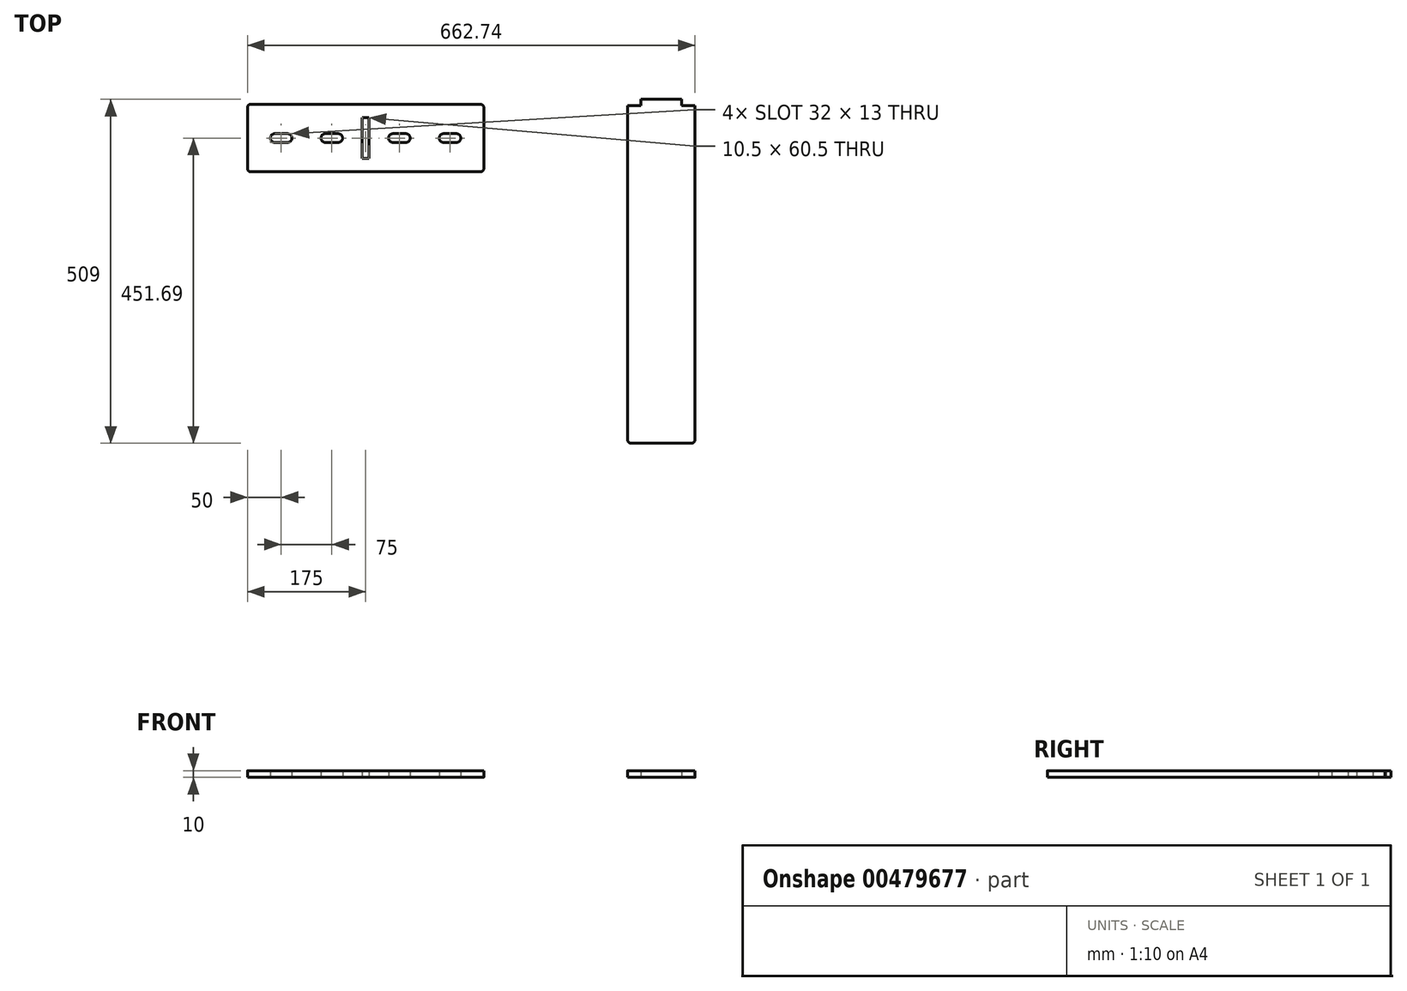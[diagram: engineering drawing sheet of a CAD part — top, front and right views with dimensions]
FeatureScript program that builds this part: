
annotation { "Feature Type Name" : "Feature", "Feature Type Description" : "" }
export const myFeature = defineFeature(function(context is Context, id is Id, definition is map)
    precondition{}
    {
        {
            var Q0;
            Q0=qCreatedBy(makeId("Top.planeOp"),FACE);
            var sketch = newSketch(context, id + "F0", { "sketchPlane" : qUnion([Q0])});
            skLineSegment(sketch, "E0.bottom", {"start": v(170, -50) * mm, "end": v(-170, -50) * mm});
            skLineSegment(sketch, "E0.top", {"start": v(170, 50) * mm, "end": v(-170, 50) * mm});
            skLineSegment(sketch, "E0.left", {"start": v(175, -45) * mm, "end": v(175, 45) * mm});
            skLineSegment(sketch, "E0.right", {"start": v(-175, -45) * mm, "end": v(-175, 45) * mm});
            skPoint(sketch, "E0.middle", {"position": v(0, 0) * mm});
            skLineSegment(sketch, "E1.bottom", {"start": v(-115.5, -6.5) * mm, "end": v(-134.5, -6.5) * mm});
            skLineSegment(sketch, "E1.top", {"start": v(-115.5, 6.5) * mm, "end": v(-134.5, 6.5) * mm});
            skPoint(sketch, "E1.middle", {"position": v(-125, 0) * mm});
            skArc(sketch, "E2", {"start": v(-134.5, 6.5) * mm, "mid": v(-141, 0) * mm, "end": v(-134.5, -6.5) * mm});
            skArc(sketch, "E3", {"start": v(-115.5, -6.5) * mm, "mid": v(-109, 0) * mm, "end": v(-115.5, 6.5) * mm});
            skLineSegment(sketch, "E4.1.0.0", {"start": v(-40.5, 6.5) * mm, "end": v(-59.5, 6.5) * mm});
            skArc(sketch, "E4.1.0.1", {"start": v(-40.5, -6.5) * mm, "mid": v(-34, 0) * mm, "end": v(-40.5, 6.5) * mm});
            skLineSegment(sketch, "E4.1.0.2", {"start": v(-40.5, -6.5) * mm, "end": v(-59.5, -6.5) * mm});
            skPoint(sketch, "E4.1.0.3", {"position": v(-50, 0) * mm});
            skArc(sketch, "E4.1.0.4", {"start": v(-59.5, 6.5) * mm, "mid": v(-66, 0) * mm, "end": v(-59.5, -6.5) * mm});
            skLineSegment(sketch, "E4.direction1", {"start": v(-134.5, -6.5) * mm, "end": v(-59.5, -6.5) * mm, "construction": true});
            skLineSegment(sketch, "E5", {"start": v(0, 50) * mm, "end": v(0, -50) * mm, "construction": true});
            skLineSegment(sketch, "E6", {"start": v(175, 0) * mm, "end": v(-175, 0) * mm, "construction": true});
            skLineSegment(sketch, "E7.bottom", {"start": v(134.5, -6.5) * mm, "end": v(115.5, -6.5) * mm});
            skLineSegment(sketch, "E7.top", {"start": v(134.5, 6.5) * mm, "end": v(115.5, 6.5) * mm});
            skPoint(sketch, "E7.middle", {"position": v(125, 0) * mm});
            skArc(sketch, "E8", {"start": v(115.5, 6.5) * mm, "mid": v(109, 0) * mm, "end": v(115.5, -6.5) * mm});
            skArc(sketch, "E9", {"start": v(134.5, -6.5) * mm, "mid": v(141, 0) * mm, "end": v(134.5, 6.5) * mm});
            skPoint(sketch, "E10.1.0.0", {"position": v(50, 0) * mm});
            skLineSegment(sketch, "E10.1.0.1", {"start": v(59.5, -6.5) * mm, "end": v(40.5, -6.5) * mm});
            skArc(sketch, "E10.1.0.2", {"start": v(59.5, -6.5) * mm, "mid": v(66, 0) * mm, "end": v(59.5, 6.5) * mm});
            skArc(sketch, "E10.1.0.3", {"start": v(40.5, 6.5) * mm, "mid": v(34, 0) * mm, "end": v(40.5, -6.5) * mm});
            skLineSegment(sketch, "E10.1.0.4", {"start": v(59.5, 6.5) * mm, "end": v(40.5, 6.5) * mm});
            skLineSegment(sketch, "E10.direction1", {"start": v(115.5, -6.5) * mm, "end": v(40.5, -6.5) * mm, "construction": true});
            skLineSegment(sketch, "E11.bottom", {"start": v(5.25, -30.25) * mm, "end": v(-5.25, -30.25) * mm});
            skLineSegment(sketch, "E11.top", {"start": v(5.25, 30.25) * mm, "end": v(-5.25, 30.25) * mm});
            skLineSegment(sketch, "E11.left", {"start": v(5.25, -30.25) * mm, "end": v(5.25, 30.25) * mm});
            skLineSegment(sketch, "E11.right", {"start": v(-5.25, -30.25) * mm, "end": v(-5.25, 30.25) * mm});
            skPoint(sketch, "E12.visualSharp", {"position": v(-175, 50) * mm});
            skArc(sketch, "E12.filletArc", {"start": v(-170, 50) * mm, "mid": v(-173.54, 48.54) * mm, "end": v(-175, 45) * mm});
            skPoint(sketch, "E13.visualSharp", {"position": v(-175, -50) * mm});
            skArc(sketch, "E13.filletArc", {"start": v(-175, -45) * mm, "mid": v(-173.54, -48.54) * mm, "end": v(-170, -50) * mm});
            skPoint(sketch, "E14.visualSharp", {"position": v(175, -50) * mm});
            skArc(sketch, "E14.filletArc", {"start": v(170, -50) * mm, "mid": v(173.54, -48.54) * mm, "end": v(175, -45) * mm});
            skPoint(sketch, "E15.visualSharp", {"position": v(175, 50) * mm});
            skArc(sketch, "E15.filletArc", {"start": v(175, 45) * mm, "mid": v(173.54, 48.54) * mm, "end": v(170, 50) * mm});
            skSolve(sketch);
        }
        {
            var Q0;
            Q0 = qSketchRegion(id + "F0", true);
            extrude(context, id + "F1", {"entities" : qUnion([Q0]), "depth" : 10 * mm, "offsetDistance" : 25 * mm});
        }
        {
            var Q0;
            Q0=qCreatedBy(makeId("Top.planeOp"),FACE);
            var sketch = newSketch(context, id + "F2", { "sketchPlane" : qUnion([Q0])});
            skLineSegment(sketch, "E16.bottom", {"start": v(387.74, 48.31) * mm, "end": v(407.74, 48.31) * mm});
            skLineSegment(sketch, "E16.top", {"start": v(392.74, -451.69) * mm, "end": v(482.74, -451.69) * mm});
            skLineSegment(sketch, "E16.left", {"start": v(387.74, 48.31) * mm, "end": v(387.74, -446.69) * mm});
            skLineSegment(sketch, "E16.right", {"start": v(487.74, 48.31) * mm, "end": v(487.74, -446.69) * mm});
            skLineSegment(sketch, "E17.top", {"start": v(407.74, 57.31) * mm, "end": v(467.74, 57.31) * mm});
            skLineSegment(sketch, "E17.left", {"start": v(407.74, 48.31) * mm, "end": v(407.74, 57.31) * mm});
            skLineSegment(sketch, "E17.right", {"start": v(467.74, 48.31) * mm, "end": v(467.74, 57.31) * mm});
            skLineSegment(sketch, "E18.trimOffspring", {"start": v(467.74, 48.31) * mm, "end": v(487.74, 48.31) * mm});
            skPoint(sketch, "E19.visualSharp", {"position": v(387.74, -451.69) * mm});
            skArc(sketch, "E19.filletArc", {"start": v(387.74, -446.69) * mm, "mid": v(389.2, -450.22) * mm, "end": v(392.74, -451.69) * mm});
            skPoint(sketch, "E20.visualSharp", {"position": v(487.74, -451.69) * mm});
            skArc(sketch, "E20.filletArc", {"start": v(482.74, -451.69) * mm, "mid": v(486.27, -450.22) * mm, "end": v(487.74, -446.69) * mm});
            skSolve(sketch);
        }
        {
            var Q0;
            Q0 = qSketchRegion(id + "F2", true);
            extrude(context, id + "F3", {"entities" : qUnion([Q0]), "depth" : 10 * mm, "offsetDistance" : 25 * mm});
        }
    });
